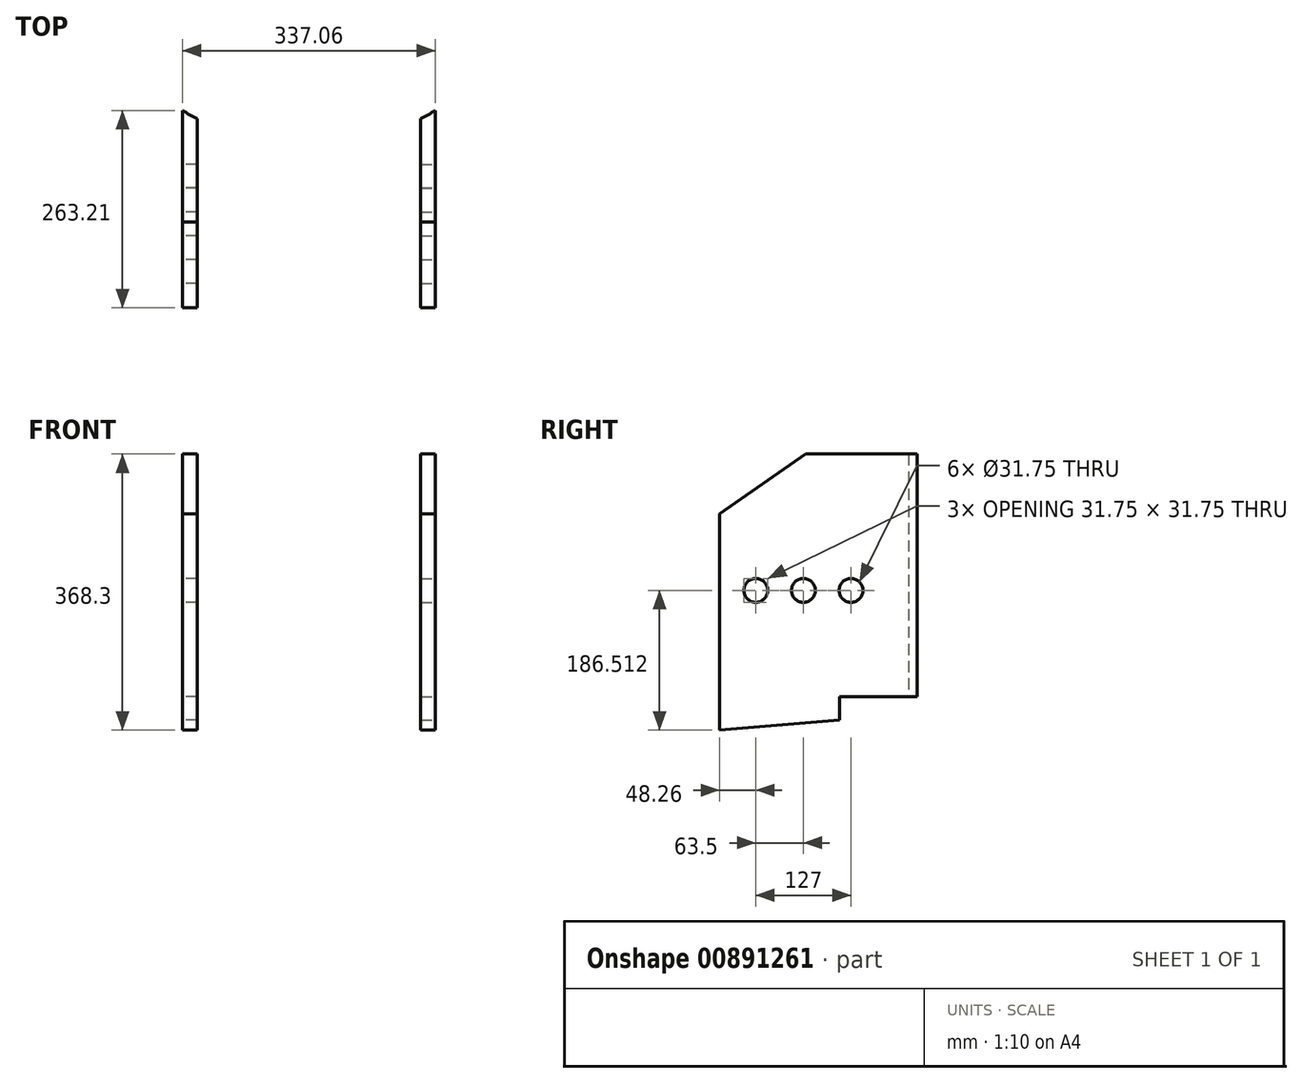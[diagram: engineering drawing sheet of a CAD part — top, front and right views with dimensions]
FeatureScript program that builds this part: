
annotation { "Feature Type Name" : "Feature", "Feature Type Description" : "" }
export const myFeature = defineFeature(function(context is Context, id is Id, definition is map)
    precondition{}
    {
        {
            var Q0;
            Q0=qCreatedBy(makeId("Top.planeOp"),FACE);
            var sketch = newSketch(context, id + "F0", { "sketchPlane" : qUnion([Q0])});
            skLineSegment(sketch, "E0", {"start": v(0, 323.85) * mm, "end": v(0, -323.85) * mm, "construction": true});
            skLineSegment(sketch, "E1", {"start": v(0, -323.85) * mm, "end": v(0, -616.17) * mm, "construction": true});
            skLineSegment(sketch, "E2", {"start": v(0, -539.75) * mm, "end": v(149.23, -539.75) * mm, "construction": true});
            skLineSegment(sketch, "E3.bottom", {"start": v(149.23, -539.75) * mm, "end": v(168.53, -539.75) * mm});
            skLineSegment(sketch, "E3.left", {"start": v(149.23, -539.75) * mm, "end": v(149.23, -287.42) * mm});
            skLineSegment(sketch, "E3.right", {"start": v(168.53, -539.75) * mm, "end": v(168.53, -276.54) * mm});
            skArc(sketch, "E4.trimOffspring", {"start": v(149.22, -287.42) * mm, "mid": v(158.97, -282.15) * mm, "end": v(168.53, -276.54) * mm});
            skSolve(sketch);
        }
        {
            var Q0;
            Q0 = qSketchRegion(id + "F0", true);
            extrude(context, id + "F1", {"entities" : qUnion([Q0]), "depth" : 323.85 * mm, "offsetDistance" : 25.4 * mm});
        }
        {
            var Q0;
            Q0=makeQuery(id+"F1.opExtrude","SWEPT_FACE",FACE,{"disambiguationData":[OSD([sQuery(id+"F0.wireOp",EDGE,"E3.right")])]});
            var sketch = newSketch(context, id + "F2", { "sketchPlane" : qUnion([Q0])});
            skLineSegment(sketch, "E5", {"start": v(-539.75, 0) * mm, "end": v(-539.75, -44.45) * mm});
            skLineSegment(sketch, "E6", {"start": v(-539.75, 0) * mm, "end": v(-379.8, 0) * mm});
            skLineSegment(sketch, "E7", {"start": v(-539.75, -44.45) * mm, "end": v(-379.8, -30.77) * mm});
            skLineSegment(sketch, "E8", {"start": v(-379.8, 0) * mm, "end": v(-379.8, -30.77) * mm});
            skSolve(sketch);
        }
        {
            var Q0;
            Q0 = qSketchRegion(id + "F2", true);
            extrude(context, id + "F3", {"entities" : qUnion([Q0]), "operationType" : NewBodyOperationType.ADD, "oppositeDirection" : true, "depth" : 19.3 * mm, "offsetDistance" : 25.4 * mm});
        }
        {
            var Q0;
            Q0=makeQuery(id+"F3.boolean.opBoolean","MERGE",FACE,{"derivedFrom":[makeQuery(id+"F1.opExtrude","SWEPT_FACE",FACE,{"disambiguationData":[OSD([sQuery(id+"F0.wireOp",EDGE,"E3.right")])]}),makeQuery(id+"F3.opExtrude","CAP_FACE",FACE,{"disambiguationData":[OSD([sQuery(id+"F2.wireOp",EDGE,"E5"),sQuery(id+"F2.wireOp",EDGE,"v0flhuXK-7psh-iCHO-cWeO-Iq2e5TEh3roq"),sQuery(id+"F2.wireOp",EDGE,"E6"),sQuery(id+"F2.wireOp",EDGE,"E7")])],"isStart":true})]});
            var sketch = newSketch(context, id + "F4", { "sketchPlane" : qUnion([Q0])});
            skLineSegment(sketch, "E9", {"start": v(-539.75, 323.85) * mm, "end": v(-424.92, 323.85) * mm});
            skLineSegment(sketch, "E10", {"start": v(-424.92, 323.85) * mm, "end": v(-539.75, 244.3) * mm});
            skLineSegment(sketch, "E11", {"start": v(-539.75, 244.3) * mm, "end": v(-539.75, 323.85) * mm});
            skCircle(sketch, "E12", {"center": v(-491.5, 142.06) * mm, "radius": 15.88 * mm});
            skCircle(sketch, "E13.1.0.0", {"center": v(-428, 142.06) * mm, "radius": 15.88 * mm});
            skCircle(sketch, "E13.2.0.0", {"center": v(-364.5, 142.06) * mm, "radius": 15.88 * mm});
            skLineSegment(sketch, "E13.direction1", {"start": v(-491.5, 142.06) * mm, "end": v(-428, 142.06) * mm, "construction": true});
            skSolve(sketch);
        }
        {
            var Q0;
            Q0 = qSketchRegion(id + "F4", true);
            extrude(context, id + "F5", {"entities" : qUnion([Q0]), "operationType" : NewBodyOperationType.REMOVE, "oppositeDirection" : true, "depth" : 83.57 * mm, "offsetDistance" : 25.4 * mm});
        }
        {
            var Q0;
            Q0=makeQuery(id+"F1.opExtrude","SWEPT_BODY",BODY,{"disambiguationData":[OSD([sQuery(id+"F0.wireOp",EDGE,"E3.bottom"),sQuery(id+"F0.wireOp",EDGE,"E3.left"),sQuery(id+"F0.wireOp",EDGE,"E3.right"),sQuery(id+"F0.wireOp",EDGE,"E4.trimOffspring")])]});
            var Q1;
            Q1=qCreatedBy(makeId("Right.planeOp"),FACE);
            mirror(context, id + "F6", {"entities" : qUnion([Q0]), "mirrorPlane" : qUnion([Q1])});
        }
    });
